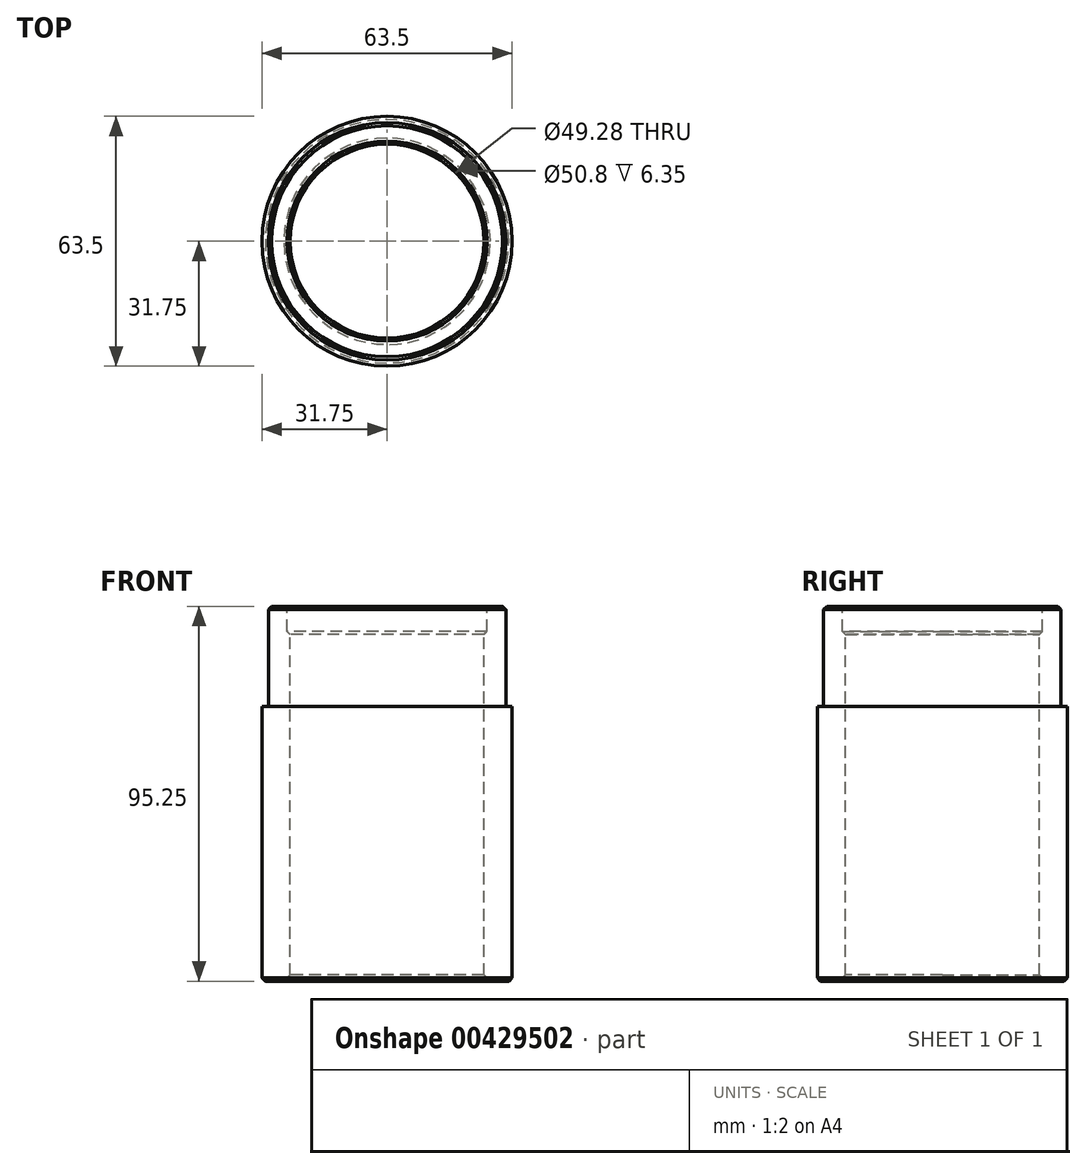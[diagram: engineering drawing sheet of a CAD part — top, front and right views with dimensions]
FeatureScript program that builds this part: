
annotation { "Feature Type Name" : "Feature", "Feature Type Description" : "" }
export const myFeature = defineFeature(function(context is Context, id is Id, definition is map)
    precondition{}
    {
        {
            var Q0;
            Q0=qCreatedBy(makeId("Top.planeOp"),FACE);
            var sketch = newSketch(context, id + "F0", { "sketchPlane" : qUnion([Q0])});
            skCircle(sketch, "E0", {"center": v(0, 0) * mm, "radius": 30.16 * mm});
            skSolve(sketch);
        }
        {
            var Q0;
            Q0 = qSketchRegion(id + "F0", true);
            extrude(context, id + "F1", {"entities" : qUnion([Q0]), "depth" : 12.7 * mm, "symmetric" : true});
        }
        {
            var Q0;
            Q0=makeQuery(id+"F1.opExtrude","CAP_FACE",FACE,{"disambiguationData":[OSD([sQuery(id+"F0.wireOp",EDGE,"E0")])],"isStart":true});
            var sketch = newSketch(context, id + "F2", { "sketchPlane" : qUnion([Q0])});
            skCircle(sketch, "E1", {"center": v(0, 0) * mm, "radius": 31.75 * mm});
            skSolve(sketch);
        }
        {
            var Q0;
            Q0 = qSketchRegion(id + "F2", true);
            extrude(context, id + "F3", {"entities" : qUnion([Q0]), "operationType" : NewBodyOperationType.ADD, "depth" : 69.85 * mm});
        }
        {
            var Q0;
            Q0=makeQuery(id+"F1.opExtrude","CAP_FACE",FACE,{"disambiguationData":[OSD([sQuery(id+"F0.wireOp",EDGE,"E0")])],"isStart":false});
            var sketch = newSketch(context, id + "F4", { "sketchPlane" : qUnion([Q0])});
            skCircle(sketch, "E2", {"center": v(0, 0) * mm, "radius": 30.16 * mm});
            skSolve(sketch);
        }
        {
            var Q0;
            Q0 = qSketchRegion(id + "F4", true);
            extrude(context, id + "F5", {"entities" : qUnion([Q0]), "operationType" : NewBodyOperationType.ADD, "depth" : 12.7 * mm});
        }
        {
            var Q0;
            Q0=makeQuery(id+"F5.opExtrude","CAP_FACE",FACE,{"disambiguationData":[OSD([sQuery(id+"F4.wireOp",EDGE,"E2")])],"isStart":false});
            var sketch = newSketch(context, id + "F6", { "sketchPlane" : qUnion([Q0])});
            skCircle(sketch, "E3", {"center": v(0, 0) * mm, "radius": 24.64 * mm});
            skSolve(sketch);
        }
        {
            var Q0;
            Q0 = qSketchRegion(id + "F6", true);
            extrude(context, id + "F7", {"entities" : qUnion([Q0]), "operationType" : NewBodyOperationType.REMOVE, "endBound" : BoundingType.THROUGH_ALL, "oppositeDirection" : true, "depth" : 25.4 * mm});
        }
        {
            var Q0;
            Q0=makeQuery(id+"F5.opExtrude","CAP_FACE",FACE,{"disambiguationData":[OSD([sQuery(id+"F4.wireOp",EDGE,"E2")])],"isStart":false});
            var sketch = newSketch(context, id + "F8", { "sketchPlane" : qUnion([Q0])});
            skCircle(sketch, "E4", {"center": v(0, 0) * mm, "radius": 25.4 * mm});
            skSolve(sketch);
        }
        {
            var Q0;
            Q0 = qSketchRegion(id + "F8", true);
            extrude(context, id + "F9", {"entities" : qUnion([Q0]), "operationType" : NewBodyOperationType.REMOVE, "oppositeDirection" : true, "depth" : 6.35 * mm});
        }
        {
            var Q0;
            Q0=makeQuery(id+"F9.boolean.opBoolean","INTERSECT",EDGE,{"derivedFrom":[makeQuery(id+"F7.boolean.opBoolean","COPY",FACE,{"derivedFrom":makeQuery(id+"F7.opExtrude","SWEPT_FACE",FACE,{"disambiguationData":[OSD([sQuery(id+"F6.wireOp",EDGE,"E3")])]})}),makeQuery(id+"F9.opExtrude","CAP_FACE",FACE,{"disambiguationData":[OSD([sQuery(id+"F8.wireOp",EDGE,"E4")])],"isStart":false})]});
            chamfer(context, id + "F10", {"entities" : qUnion([Q0]), "width" : 0.76 * mm, "tangentPropagation" : true});
        }
        {
            var Q0;
            Q0=makeQuery(id+"F7.boolean.opBoolean","INTERSECT",EDGE,{"derivedFrom":[makeQuery(id+"F3.opExtrude","CAP_FACE",FACE,{"disambiguationData":[OSD([sQuery(id+"F2.wireOp",EDGE,"E1")])],"isStart":false}),makeQuery(id+"F7.opExtrude","SWEPT_FACE",FACE,{"disambiguationData":[OSD([sQuery(id+"F6.wireOp",EDGE,"E3")])]})]});
            chamfer(context, id + "F11", {"entities" : qUnion([Q0]), "width" : 1.59 * mm, "tangentPropagation" : true});
        }
        {
            var Q0;
            Q0=makeQuery(id+"F3.opExtrude","CAP_EDGE",EDGE,{"disambiguationData":[OSD([sQuery(id+"F2.wireOp",EDGE,"E1")])],"isStart":false});
            var Q1;
            Q1=makeQuery(id+"F5.opExtrude","CAP_EDGE",EDGE,{"disambiguationData":[OSD([sQuery(id+"F4.wireOp",EDGE,"E2")])],"isStart":false});
            chamfer(context, id + "F12", {"entities" : qUnion([Q0, Q1]), "width" : 0.83 * mm, "tangentPropagation" : true});
        }
    });
